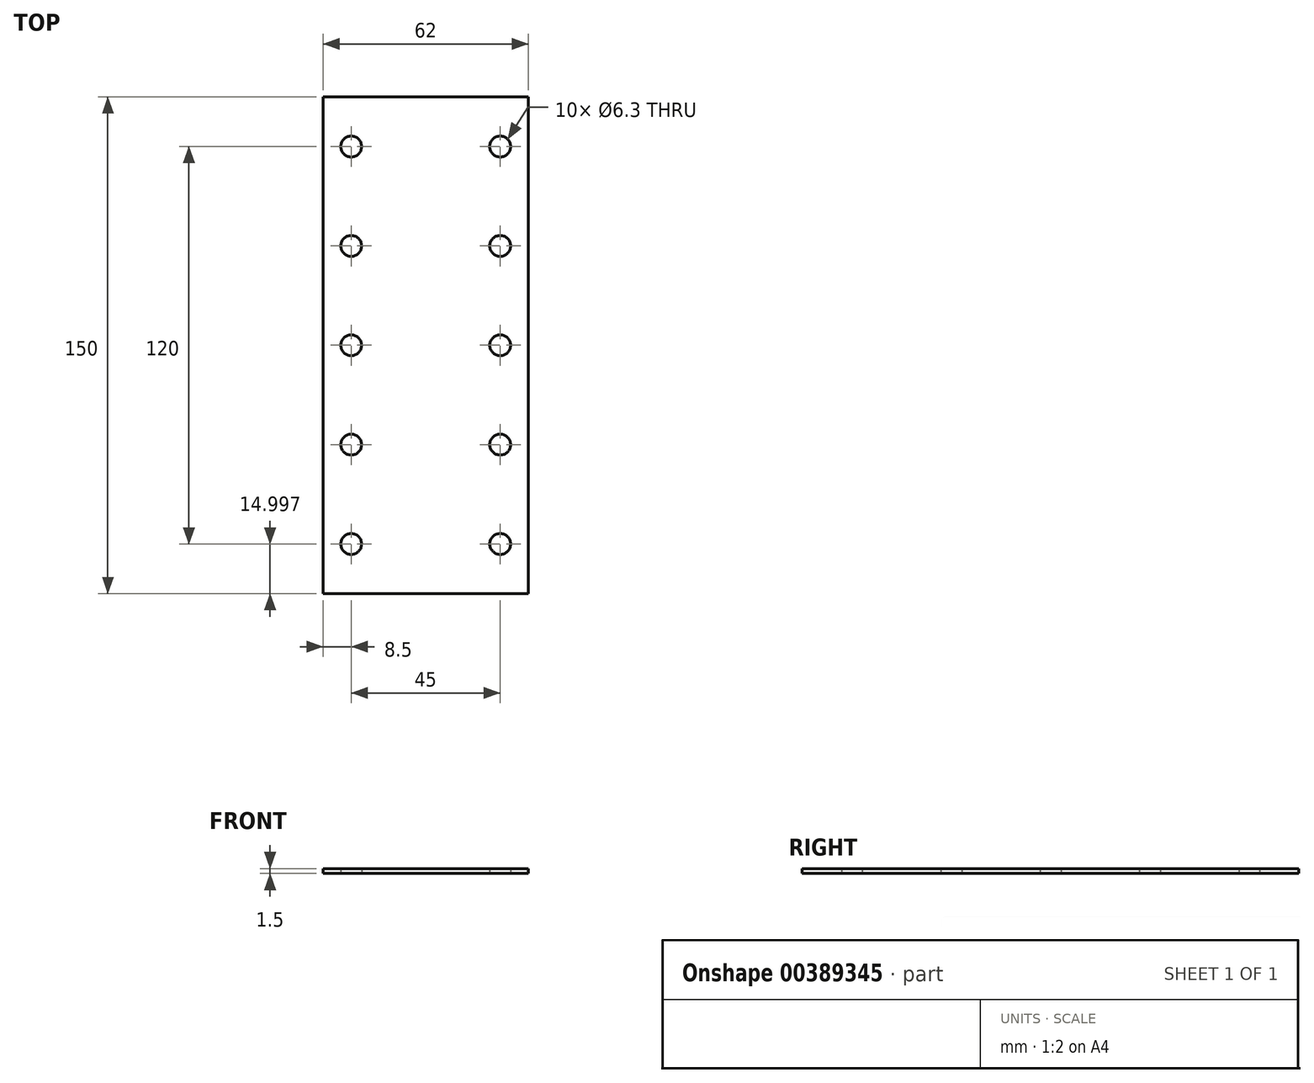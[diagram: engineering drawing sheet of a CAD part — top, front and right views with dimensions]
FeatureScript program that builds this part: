
annotation { "Feature Type Name" : "Feature", "Feature Type Description" : "" }
export const myFeature = defineFeature(function(context is Context, id is Id, definition is map)
    precondition{}
    {
        {
            var Q0;
            Q0=qCreatedBy(makeId("Top.planeOp"),FACE);
            var sketch = newSketch(context, id + "F0", { "sketchPlane" : qUnion([Q0])});
            skLineSegment(sketch, "E0.bottom", {"start": v(32, 81.05) * mm, "end": v(-30, 81.05) * mm});
            skLineSegment(sketch, "E0.top", {"start": v(32, -68.95) * mm, "end": v(-30, -68.95) * mm});
            skLineSegment(sketch, "E0.left", {"start": v(32, 81.05) * mm, "end": v(32, -68.95) * mm});
            skLineSegment(sketch, "E0.right", {"start": v(-30, 81.05) * mm, "end": v(-30, -68.95) * mm});
            skPoint(sketch, "E0.middle", {"position": v(1, 6.05) * mm});
            skLineSegment(sketch, "E1.bottom", {"start": v(-3, 81.05) * mm, "end": v(5, 81.05) * mm});
            skLineSegment(sketch, "E1.top", {"start": v(-3, -68.95) * mm, "end": v(5, -68.95) * mm});
            skCircle(sketch, "E2", {"center": v(-21.5, 66.05) * mm, "radius": 3.15 * mm});
            skCircle(sketch, "E3", {"center": v(23.5, 66.05) * mm, "radius": 3.15 * mm});
            skCircle(sketch, "E4", {"center": v(23.5, 36.05) * mm, "radius": 3.15 * mm});
            skCircle(sketch, "E5", {"center": v(-21.5, 36.05) * mm, "radius": 3.15 * mm});
            skCircle(sketch, "E6", {"center": v(-21.5, 6.05) * mm, "radius": 3.15 * mm});
            skCircle(sketch, "E7", {"center": v(23.5, 6.05) * mm, "radius": 3.15 * mm});
            skCircle(sketch, "E8", {"center": v(-21.5, -23.95) * mm, "radius": 3.15 * mm});
            skCircle(sketch, "E9", {"center": v(23.5, -23.95) * mm, "radius": 3.15 * mm});
            skCircle(sketch, "E10", {"center": v(23.5, -53.95) * mm, "radius": 3.15 * mm});
            skCircle(sketch, "E11", {"center": v(-21.5, -53.95) * mm, "radius": 3.15 * mm});
            skSolve(sketch);
        }
        {
            var Q0;
            Q0 = qSketchRegion(id + "F0", true);
            extrude(context, id + "F1", {"entities" : qUnion([Q0]), "depth" : 1.5 * mm, "offsetDistance" : 25 * mm});
        }
    });
